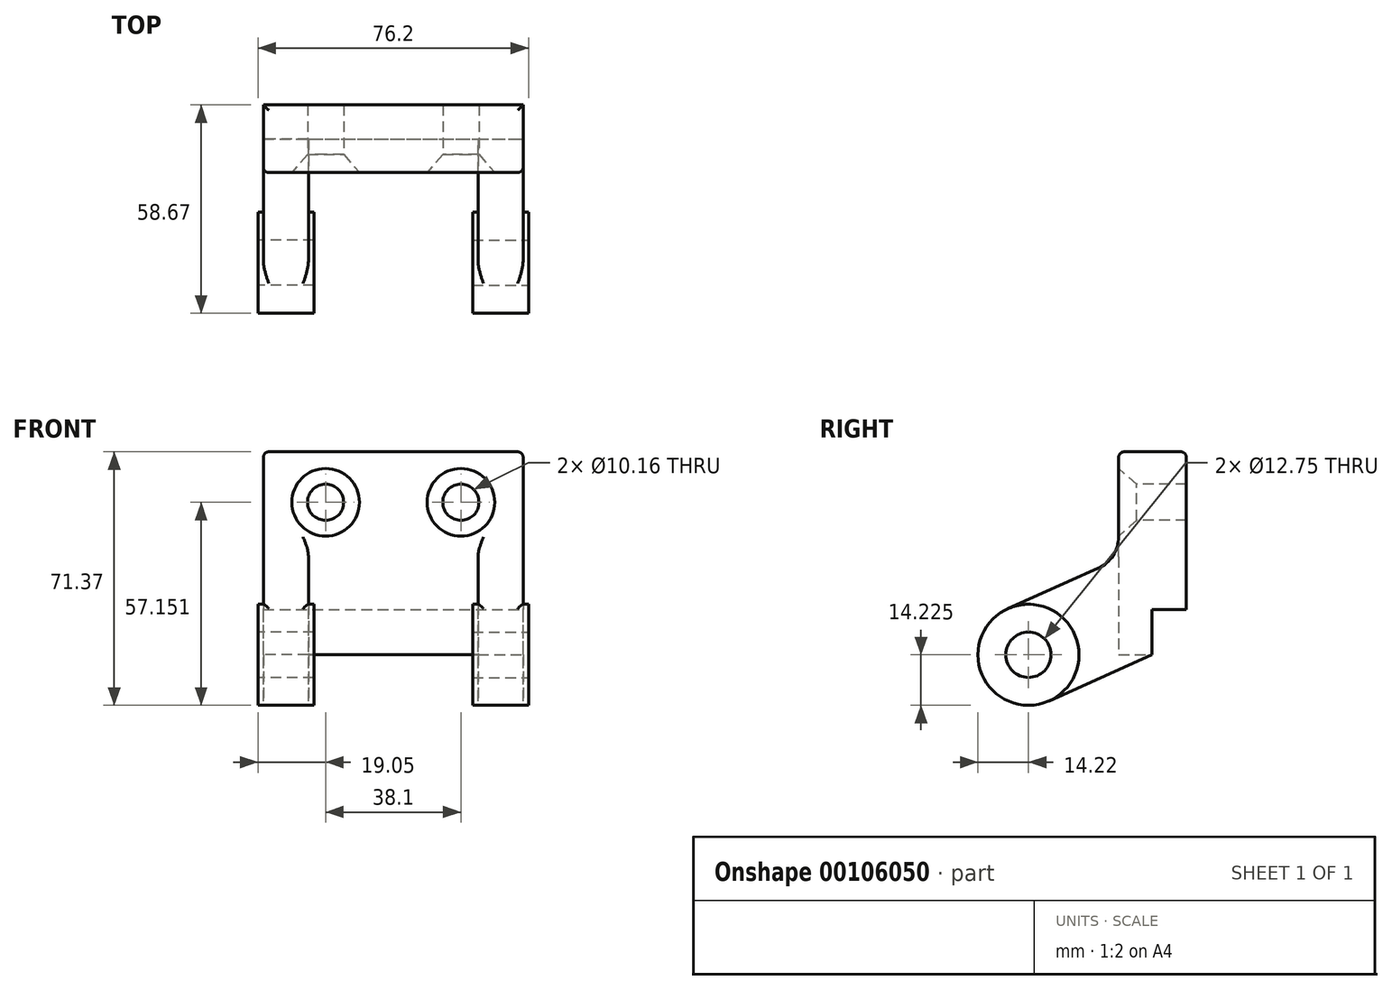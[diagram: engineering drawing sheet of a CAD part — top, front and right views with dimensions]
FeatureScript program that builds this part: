
annotation { "Feature Type Name" : "Feature", "Feature Type Description" : "" }
export const myFeature = defineFeature(function(context is Context, id is Id, definition is map)
    precondition{}
    {
        {
            var Q0;
            Q0=qCreatedBy(makeId("Front.planeOp"),FACE);
            var sketch = newSketch(context, id + "F0", { "sketchPlane" : qUnion([Q0])});
            skLineSegment(sketch, "E0.bottom", {"start": v(36.58, 28.58) * mm, "end": v(-36.58, 28.58) * mm});
            skLineSegment(sketch, "E0.top", {"start": v(36.58, -28.58) * mm, "end": v(-36.58, -28.58) * mm});
            skLineSegment(sketch, "E0.left", {"start": v(36.58, 28.58) * mm, "end": v(36.58, -28.58) * mm});
            skLineSegment(sketch, "E0.right", {"start": v(-36.58, 28.58) * mm, "end": v(-36.58, -28.58) * mm});
            skPoint(sketch, "E0.middle", {"position": v(0, 0) * mm});
            skSolve(sketch);
        }
        {
            var Q0;
            Q0=makeQuery(id+"F0.imprint","IMPRINT",FACE,{"disambiguationData":[TD([[makeQuery(id+"F0.imprint","IMPRINT",EDGE,{"derivedFrom":sQuery(id+"F0.wireOp",EDGE,"E0.bottom")}),1.0]])]});
            extrude(context, id + "F1", {"entities" : qUnion([Q0]), "depth" : 19.05 * mm});
        }
        {
            var Q0;
            Q0=makeQuery(id+"F1.opExtrude","SWEPT_FACE",FACE,{"disambiguationData":[OSD([sQuery(id+"F0.wireOp",EDGE,"E0.left")])]});
            var sketch = newSketch(context, id + "F2", { "sketchPlane" : qUnion([Q0])});
            skLineSegment(sketch, "E1.bottom", {"start": v(0, -28.57) * mm, "end": v(-9.65, -28.57) * mm});
            skLineSegment(sketch, "E1.top", {"start": v(0, -15.87) * mm, "end": v(-9.65, -15.87) * mm});
            skLineSegment(sketch, "E1.left", {"start": v(0, -28.57) * mm, "end": v(0, -15.87) * mm});
            skLineSegment(sketch, "E1.right", {"start": v(-9.65, -28.57) * mm, "end": v(-9.65, -15.87) * mm});
            skSolve(sketch);
        }
        {
            var Q0;
            Q0=makeQuery(id+"F2.imprint","IMPRINT",FACE,{"disambiguationData":[TD([[makeQuery(id+"F2.imprint","IMPRINT",EDGE,{"derivedFrom":sQuery(id+"F2.wireOp",EDGE,"E1.bottom")}),1.0]])]});
            extrude(context, id + "F3", {"entities" : qUnion([Q0]), "operationType" : NewBodyOperationType.REMOVE, "oppositeDirection" : true, "depth" : 73.15 * mm});
        }
        {
            var Q0;
            Q0=makeQuery(id+"F1.opExtrude","SWEPT_FACE",FACE,{"disambiguationData":[OSD([sQuery(id+"F0.wireOp",EDGE,"E0.left")])]});
            var sketch = newSketch(context, id + "F4", { "sketchPlane" : qUnion([Q0])});
            skLineSegment(sketch, "E2", {"start": v(0, -28.58) * mm, "end": v(-44.45, -28.58) * mm});
            skPoint(sketch, "E3", {"position": v(-44.45, -28.58) * mm});
            skCircle(sketch, "E4", {"center": v(-44.45, -28.58) * mm, "radius": 14.22 * mm});
            skLineSegment(sketch, "E5", {"start": v(-9.65, -28.58) * mm, "end": v(-38.64, -41.56) * mm});
            skLineSegment(sketch, "E6", {"start": v(-38.64, -41.56) * mm, "end": v(-50.26, -15.6) * mm});
            skLineSegment(sketch, "E7", {"start": v(-50.26, -15.6) * mm, "end": v(-24.76, -4.17) * mm});
            skLineSegment(sketch, "E8", {"start": v(-19.05, 4.64) * mm, "end": v(-19.05, 28.58) * mm});
            skPoint(sketch, "E9.visualSharp", {"position": v(-19.05, -1.61) * mm});
            skArc(sketch, "E9.filletArc", {"start": v(-24.76, -4.17) * mm, "mid": v(-20.6, -0.6) * mm, "end": v(-19.05, 4.64) * mm});
            skSolve(sketch);
        }
        {
            var Q0;
            {var subQ5=sQuery(id+"F4.wireOp",EDGE,"E7");Q0=makeQuery(id+"F4.imprint","IMPRINT",FACE,{"disambiguationData":[TD([[makeQuery(id+"F4.imprint","IMPRINT",EDGE,{"derivedFrom":subQ5}),-1.0]])]});}
            var Q1;
            {var subQ0=sQuery(id+"F4.wireOp",EDGE,"E6");var subQ1=sQuery(id+"F4.wireOp",EDGE,"E2");var subQ2=makeQuery(id+"F4.imprint","INTERSECT",VERTEX,{"derivedFrom":[subQ1,subQ0]});Q1=makeQuery(id+"F4.imprint","IMPRINT",FACE,{"disambiguationData":[TD([[makeQuery(id+"F4.imprint","IMPRINT",EDGE,{"disambiguationData":[TD([[subQ2,1.0]])],"derivedFrom":subQ1}),-1.0]])]});}
            var Q2;
            {var subQ0=sQuery(id+"F4.wireOp",EDGE,"E6");var subQ1=sQuery(id+"F4.wireOp",EDGE,"E2");var subQ2=makeQuery(id+"F4.imprint","INTERSECT",VERTEX,{"derivedFrom":[subQ1,subQ0]});Q2=makeQuery(id+"F4.imprint","IMPRINT",FACE,{"disambiguationData":[TD([[makeQuery(id+"F4.imprint","IMPRINT",EDGE,{"disambiguationData":[TD([[subQ2,1.0]])],"derivedFrom":subQ1}),1.0]])]});}
            var Q3;
            {var subQ2=sQuery(id+"F4.wireOp",EDGE,"E5");Q3=makeQuery(id+"F4.imprint","IMPRINT",FACE,{"disambiguationData":[TD([[makeQuery(id+"F4.imprint","IMPRINT",EDGE,{"derivedFrom":subQ2}),-1.0]])]});}
            extrude(context, id + "F5", {"entities" : qUnion([Q0, Q1, Q2, Q3]), "operationType" : NewBodyOperationType.ADD, "oppositeDirection" : true, "depth" : 12.7 * mm});
        }
        {
            var Q0;
            {var subQ0=sQuery(id+"F0.wireOp",EDGE,"E0.left");Q0=makeQuery(id+"F5.boolean.opBoolean","MERGE",FACE,{"derivedFrom":[makeQuery(id+"F1.opExtrude","SWEPT_FACE",FACE,{"disambiguationData":[OSD([subQ0])]}),makeQuery(id+"F5.opExtrude","CAP_FACE",FACE,{"disambiguationData":[OSD([subQ0,sQuery(id+"F4.wireOp",EDGE,"E2"),sQuery(id+"F4.wireOp",EDGE,"E5"),sQuery(id+"F4.wireOp",EDGE,"E6"),sQuery(id+"F4.wireOp",EDGE,"E7")])],"isStart":true})]});}
            var sketch = newSketch(context, id + "F6", { "sketchPlane" : qUnion([Q0])});
            skCircle(sketch, "E10", {"center": v(-44.45, -28.57) * mm, "radius": 14.22 * mm});
            skSolve(sketch);
        }
        {
            var Q0;
            {var subQ1=makeQuery(id+"F5.opExtrude","CAP_EDGE",EDGE,{"disambiguationData":[OSD([sQuery(id+"F4.wireOp",EDGE,"E6")])],"isStart":true});Q0=makeQuery(id+"F6.imprint","IMPRINT",FACE,{"disambiguationData":[TD([[makeQuery(id+"F6.imprint","IMPRINT",EDGE,{"derivedFrom":subQ1}),1.0]])]});}
            extrude(context, id + "F7", {"entities" : qUnion([Q0]), "operationType" : NewBodyOperationType.ADD, "oppositeDirection" : true, "depth" : 14.22 * mm});
        }
        {
            var Q0;
            {var subQ0=sQuery(id+"F4.wireOp",EDGE,"E6");var subQ1=sQuery(id+"F0.wireOp",EDGE,"E0.left");Q0=makeQuery(id+"F7.boolean.opBoolean","MERGE",FACE,{"derivedFrom":[makeQuery(id+"F5.boolean.opBoolean","MERGE",FACE,{"derivedFrom":[makeQuery(id+"F1.opExtrude","SWEPT_FACE",FACE,{"disambiguationData":[OSD([subQ1])]}),makeQuery(id+"F5.opExtrude","CAP_FACE",FACE,{"disambiguationData":[OSD([subQ1,sQuery(id+"F4.wireOp",EDGE,"E2"),sQuery(id+"F4.wireOp",EDGE,"E5"),subQ0,sQuery(id+"F4.wireOp",EDGE,"E7")])],"isStart":true})]}),makeQuery(id+"F7.opExtrude","CAP_FACE",FACE,{"disambiguationData":[OSD([subQ0,sQuery(id+"F6.wireOp",EDGE,"E10")])],"isStart":true})]});}
            var sketch = newSketch(context, id + "F8", { "sketchPlane" : qUnion([Q0])});
            skCircle(sketch, "E11", {"center": v(-44.45, -28.58) * mm, "radius": 14.22 * mm});
            skSolve(sketch);
        }
        {
            var Q0;
            {var subQ0=sQuery(id+"F8.wireOp",EDGE,"E11");var subQ1=makeQuery(id+"F8.imprint","INTERSECT",VERTEX,{"derivedFrom":[makeQuery(id+"F5.opExtrude","CAP_EDGE",EDGE,{"disambiguationData":[OSD([sQuery(id+"F4.wireOp",EDGE,"E5")])],"isStart":true}),subQ0]});Q0=makeQuery(id+"F8.imprint","IMPRINT",FACE,{"disambiguationData":[TD([[makeQuery(id+"F8.imprint","IMPRINT",EDGE,{"disambiguationData":[TD([[subQ1,1.0]])],"derivedFrom":subQ0}),1.0]])]});}
            extrude(context, id + "F9", {"entities" : qUnion([Q0]), "operationType" : NewBodyOperationType.ADD, "depth" : 1.52 * mm});
        }
        {
            var Q0;
            Q0=makeQuery(id+"F1.opExtrude","CAP_FACE",FACE,{"disambiguationData":[OSD([sQuery(id+"F0.wireOp",EDGE,"E0.bottom"),sQuery(id+"F0.wireOp",EDGE,"E0.top"),sQuery(id+"F0.wireOp",EDGE,"E0.left"),sQuery(id+"F0.wireOp",EDGE,"E0.right")])],"isStart":false});
            var sketch = newSketch(context, id + "F10", { "sketchPlane" : qUnion([Q0])});
            skLineSegment(sketch, "E12", {"start": v(19.05, -28.58) * mm, "end": v(19.05, 14.35) * mm});
            skLineSegment(sketch, "E13", {"start": v(19.05, 14.35) * mm, "end": v(36.58, 14.35) * mm});
            skPoint(sketch, "E14", {"position": v(19.05, 14.35) * mm});
            skLineSegment(sketch, "E15.bottom", {"start": v(-36.58, 28.58) * mm, "end": v(0, 28.58) * mm});
            skLineSegment(sketch, "E15.top", {"start": v(-36.58, -28.58) * mm, "end": v(0, -28.58) * mm});
            skLineSegment(sketch, "E15.left", {"start": v(-36.58, 28.58) * mm, "end": v(-36.58, -28.58) * mm});
            skLineSegment(sketch, "E15.right", {"start": v(0, 28.58) * mm, "end": v(0, -28.58) * mm});
            skSolve(sketch);
        }
        {
            var Q0;
            Q0=makeQuery(id+"F9.opExtrude","CAP_FACE",FACE,{"disambiguationData":[OSD([sQuery(id+"F8.wireOp",EDGE,"E11")])],"isStart":false});
            var sketch = newSketch(context, id + "F11", { "sketchPlane" : qUnion([Q0])});
            skPoint(sketch, "E16", {"position": v(-44.45, -28.58) * mm});
            skSolve(sketch);
        }
        {
            var Q0;
            Q0=sQuery(id+"F10.wireOp",VERTEX,"E14");
            var Q1;
            Q1=makeQuery(id+"F1.opExtrude","SWEPT_BODY",BODY,{"disambiguationData":[OSD([sQuery(id+"F0.wireOp",EDGE,"E0.bottom"),sQuery(id+"F0.wireOp",EDGE,"E0.top"),sQuery(id+"F0.wireOp",EDGE,"E0.left"),sQuery(id+"F0.wireOp",EDGE,"E0.right")])]});
            hole(context, id + "F12", {"style" : HoleStyle.C_SINK, "endStyle" : HoleEndStyle.THROUGH, "holeDiameter" : 10.16 * mm, "cSinkDiameter" : 19.05 * mm, "cSinkAngle" : 82 * degree, "locations" : qUnion([Q0]), "scope" : qUnion([Q1]), "isTappedThrough" : true});
        }
        {
            var Q0;
            {var subQ0=sQuery(id+"F8.wireOp",EDGE,"E11");var subQ1=makeQuery(id+"F8.imprint","INTERSECT",VERTEX,{"derivedFrom":[makeQuery(id+"F5.opExtrude","CAP_EDGE",EDGE,{"disambiguationData":[OSD([sQuery(id+"F4.wireOp",EDGE,"E5")])],"isStart":true}),subQ0]});Q0=makeQuery(id+"F8.imprint","IMPRINT",FACE,{"disambiguationData":[TD([[makeQuery(id+"F8.imprint","IMPRINT",EDGE,{"disambiguationData":[TD([[subQ1,1.0]])],"derivedFrom":subQ0}),1.0]])]});}
            extrude(context, id + "F13", {"entities" : qUnion([Q0]), "operationType" : NewBodyOperationType.ADD, "oppositeDirection" : true, "depth" : 14.22 * mm});
        }
        {
            var Q0;
            Q0=sQuery(id+"F11.wireOp",VERTEX,"E16");
            var Q1;
            Q1=makeQuery(id+"F1.opExtrude","SWEPT_BODY",BODY,{"disambiguationData":[OSD([sQuery(id+"F0.wireOp",EDGE,"E0.bottom"),sQuery(id+"F0.wireOp",EDGE,"E0.top"),sQuery(id+"F0.wireOp",EDGE,"E0.left"),sQuery(id+"F0.wireOp",EDGE,"E0.right")])]});
            hole(context, id + "F14", {"style" : HoleStyle.SIMPLE, "endStyle" : HoleEndStyle.THROUGH, "holeDiameter" : 12.75 * mm, "locations" : qUnion([Q0]), "scope" : qUnion([Q1]), "isTappedThrough" : true});
        }
        {
            var Q0;
            Q0=makeQuery(id+"F1.opExtrude","CAP_EDGE",EDGE,{"disambiguationData":[OSD([sQuery(id+"F0.wireOp",EDGE,"E0.bottom")])],"isStart":false});
            var Q1;
            Q1=makeQuery(id+"F1.opExtrude","CAP_EDGE",EDGE,{"disambiguationData":[OSD([sQuery(id+"F0.wireOp",EDGE,"E0.bottom")])],"isStart":true});
            var Q2;
            Q2=makeQuery(id+"F5.opExtrude","CAP_EDGE",EDGE,{"disambiguationData":[OSD([sQuery(id+"F4.wireOp",EDGE,"E7")])],"isStart":false});
            var Q3;
            Q3=makeQuery(id+"F5.opExtrude","CAP_EDGE",EDGE,{"disambiguationData":[OSD([sQuery(id+"F4.wireOp",EDGE,"E7")])],"isStart":true});
            var Q4;
            Q4=makeQuery(id+"F5.opExtrude","CAP_EDGE",EDGE,{"disambiguationData":[OSD([sQuery(id+"F0.wireOp",EDGE,"E0.left")])],"isStart":false});
            var Q5;
            Q5=makeQuery(id+"F1.opExtrude","SWEPT_EDGE",EDGE,{"disambiguationData":[OSD([sQuery(id+"F0.wireOp",EDGE,"E0.bottom"),sQuery(id+"F0.wireOp",EDGE,"E0.left")])]});
            var Q6;
            Q6=makeQuery(id+"F1.opExtrude","SWEPT_EDGE",EDGE,{"disambiguationData":[OSD([sQuery(id+"F0.wireOp",EDGE,"E0.bottom"),sQuery(id+"F0.wireOp",EDGE,"E0.right")])]});
            fillet(context, id + "F15", {"entities" : qUnion([Q0, Q1, Q2, Q3, Q4, Q5, Q6]), "radius" : 1.52 * mm, "tangentPropagation" : true, "allowEdgeOverflow" : false});
        }
        {
            var Q0;
            Q0=makeQuery(id+"F10.imprint","IMPRINT",FACE,{"disambiguationData":[TD([[makeQuery(id+"F10.imprint","IMPRINT",EDGE,{"derivedFrom":sQuery(id+"F10.wireOp",EDGE,"E15.bottom")}),1.0]])]});
            extrude(context, id + "F16", {"entities" : qUnion([Q0]), "operationType" : NewBodyOperationType.REMOVE, "oppositeDirection" : true, "depth" : 25.4 * mm});
        }
        {
            var Q0;
            Q0=makeQuery(id+"F1.opExtrude","SWEPT_BODY",BODY,{"disambiguationData":[OSD([sQuery(id+"F0.wireOp",EDGE,"E0.bottom"),sQuery(id+"F0.wireOp",EDGE,"E0.top"),sQuery(id+"F0.wireOp",EDGE,"E0.left"),sQuery(id+"F0.wireOp",EDGE,"E0.right")])]});
            var Q1;
            Q1=qCreatedBy(makeId("Right.planeOp"),FACE);
            mirror(context, id + "F17", {"operationType" : NewBodyOperationType.ADD, "entities" : qUnion([Q0]), "mirrorPlane" : qUnion([Q1])});
        }
    });
